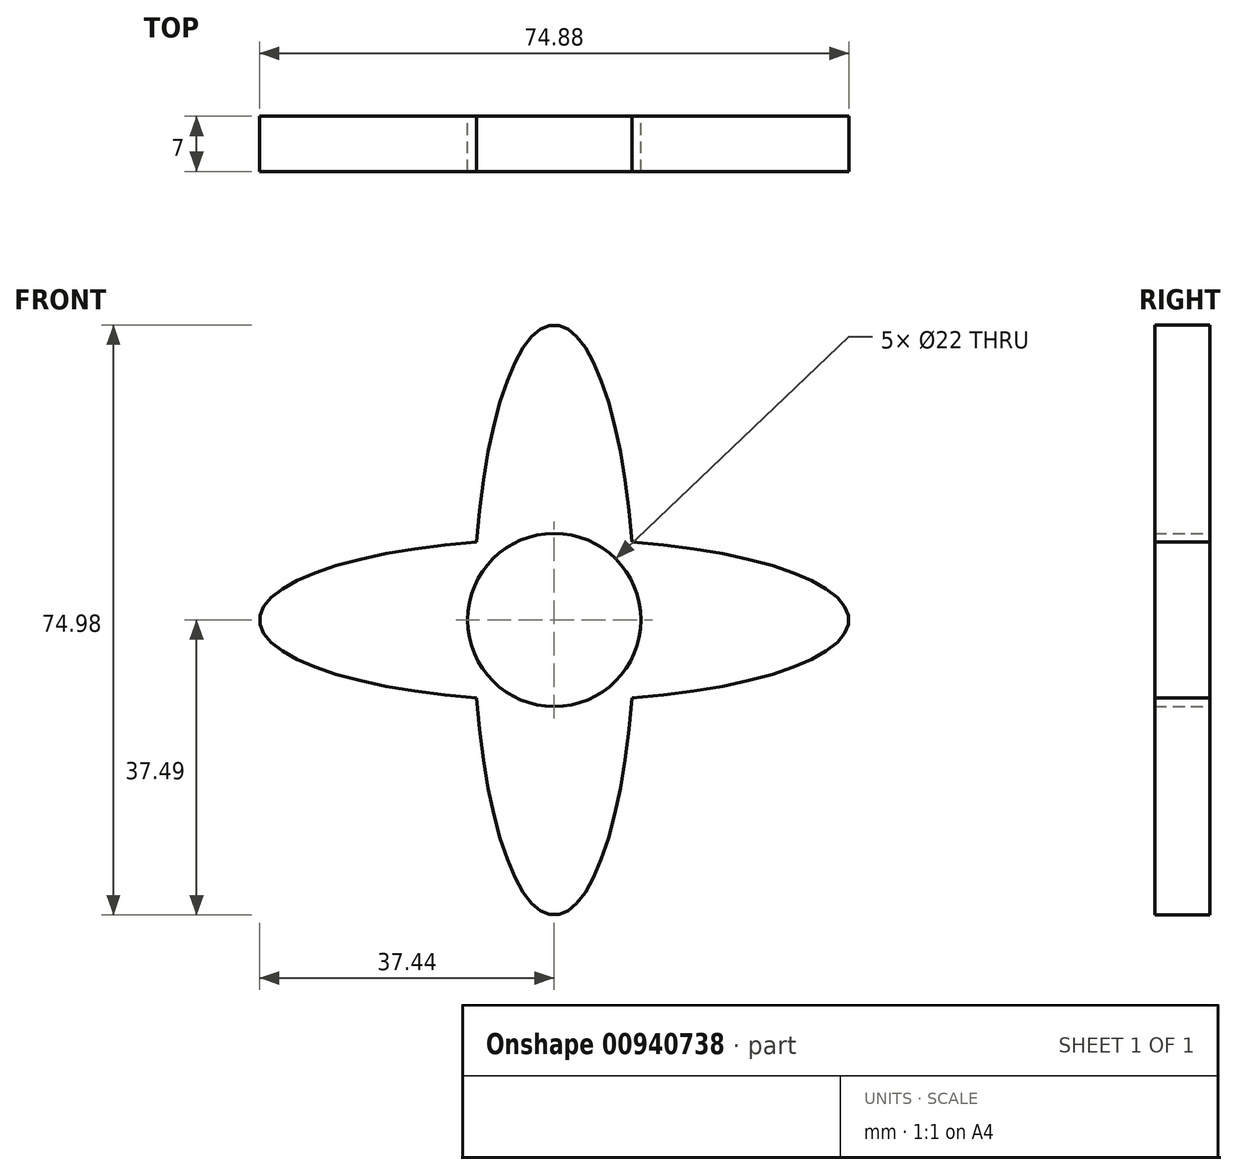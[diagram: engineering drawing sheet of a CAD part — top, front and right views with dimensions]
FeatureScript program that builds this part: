
annotation { "Feature Type Name" : "Feature", "Feature Type Description" : "" }
export const myFeature = defineFeature(function(context is Context, id is Id, definition is map)
    precondition{}
    {
        {
            var Q0;
            Q0=qCreatedBy(makeId("Front.planeOp"),FACE);
            var sketch = newSketch(context, id + "F0", { "sketchPlane" : qUnion([Q0])});
            skCircle(sketch, "E0", {"center": v(0, 0) * mm, "radius": 11 * mm});
            skEllipse(sketch, "E1", {"center": v(0, 0) * mm, "majorRadius": 37.49 * mm, "minorRadius": 10.21 * mm, "majorAxis": v(0, 1)});
            skEllipse(sketch, "E2", {"center": v(0, 0) * mm, "majorRadius": 37.44 * mm, "minorRadius": 10.26 * mm, "majorAxis": v(1, 0)});
            skSolve(sketch);
        }
        {
            var Q0;
            Q0 = qSketchRegion(id + "F0", true);
            extrude(context, id + "F1", {"entities" : qUnion([Q0]), "depth" : 7 * mm, "offsetDistance" : 25 * mm});
        }
    });
